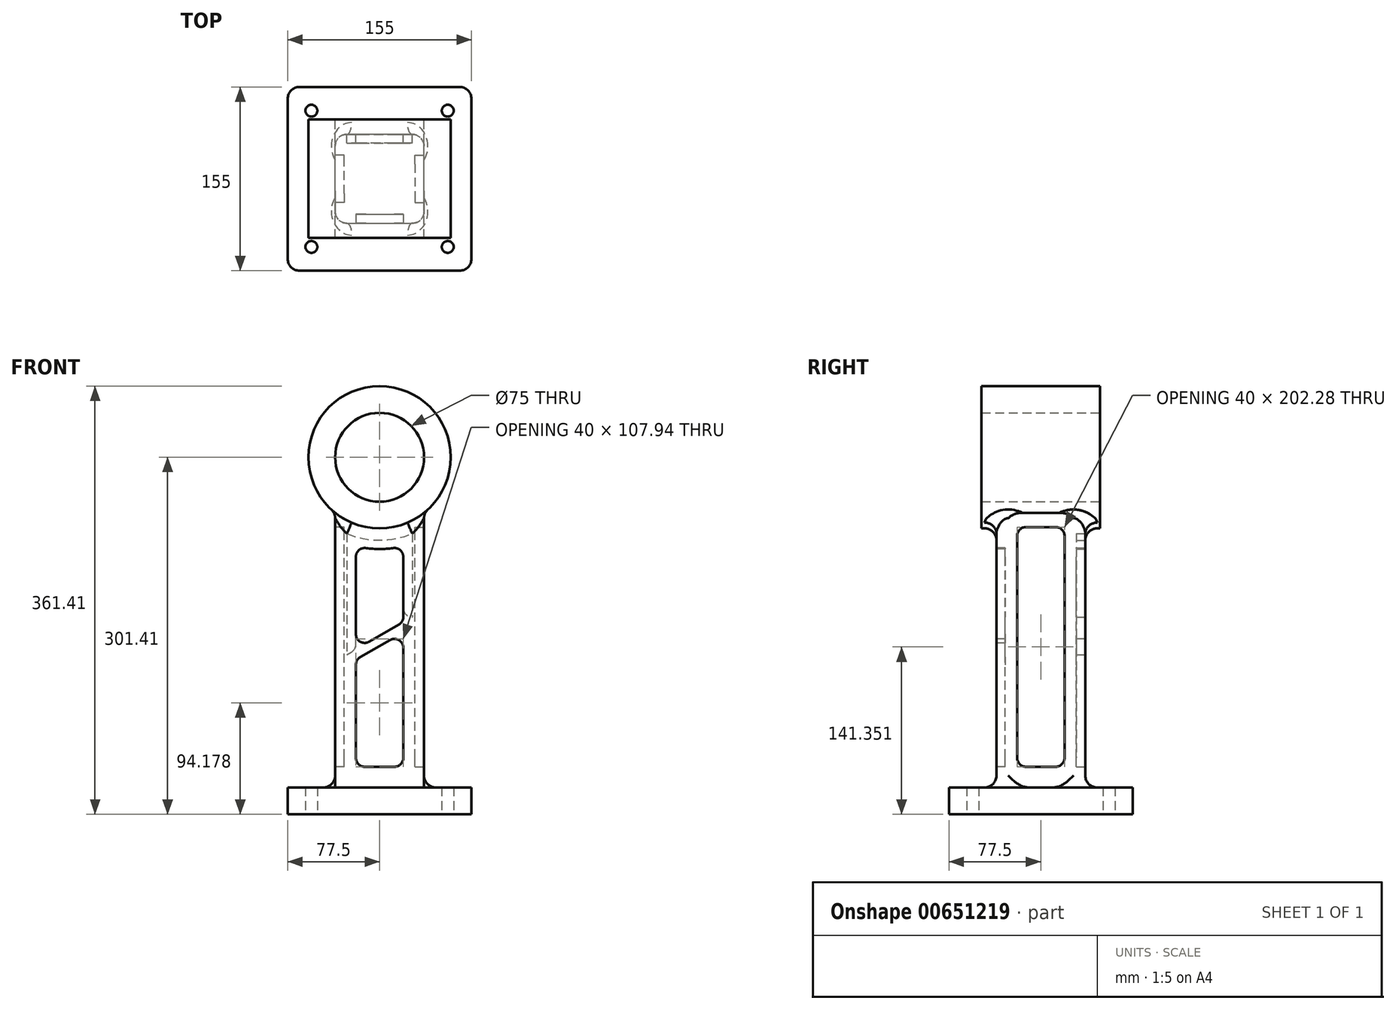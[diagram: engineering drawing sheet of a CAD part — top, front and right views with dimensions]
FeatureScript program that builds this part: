
annotation { "Feature Type Name" : "Feature", "Feature Type Description" : "" }
export const myFeature = defineFeature(function(context is Context, id is Id, definition is map)
    precondition{}
    {
        {
            var Q0;
            Q0=qCreatedBy(makeId("Front.planeOp"),FACE);
            var sketch = newSketch(context, id + "F0", { "sketchPlane" : qUnion([Q0])});
            skCircle(sketch, "E0", {"center": v(0, 0) * mm, "radius": 37.5 * mm});
            skCircle(sketch, "E1", {"center": v(0, 0) * mm, "radius": 60 * mm});
            skPoint(sketch, "E2", {"position": v(-37.5, 0) * mm});
            skPoint(sketch, "E3", {"position": v(37.5, 0) * mm});
            skPoint(sketch, "E4", {"position": v(-37.5, -46.84) * mm});
            skPoint(sketch, "E5", {"position": v(37.5, -46.84) * mm});
            skLineSegment(sketch, "E6", {"start": v(-37.5, -46.84) * mm, "end": v(-37.5, -278.7) * mm});
            skLineSegment(sketch, "E7", {"start": v(37.5, -46.84) * mm, "end": v(37.5, -278.7) * mm});
            skLineSegment(sketch, "E8", {"start": v(-37.5, -301.4) * mm, "end": v(37.5, -301.4) * mm});
            skLineSegment(sketch, "E9", {"start": v(37.5, -301.4) * mm, "end": v(77.5, -301.4) * mm});
            skLineSegment(sketch, "E10", {"start": v(77.5, -301.4) * mm, "end": v(77.5, -278.7) * mm});
            skLineSegment(sketch, "E11", {"start": v(77.5, -278.7) * mm, "end": v(37.5, -278.7) * mm});
            skLineSegment(sketch, "E12", {"start": v(37.5, -278.7) * mm, "end": v(-37.5, -278.7) * mm});
            skLineSegment(sketch, "E13", {"start": v(-37.5, -278.7) * mm, "end": v(-77.5, -278.7) * mm});
            skLineSegment(sketch, "E14", {"start": v(-77.5, -278.7) * mm, "end": v(-77.5, -301.4) * mm});
            skLineSegment(sketch, "E15", {"start": v(-77.5, -301.4) * mm, "end": v(-37.5, -301.4) * mm});
            skSolve(sketch);
        }
        {
            var Q0;
            Q0=makeQuery(id+"F0.imprint","IMPRINT",FACE,{"disambiguationData":[TD([[makeQuery(id+"F0.imprint","IMPRINT",EDGE,{"derivedFrom":sQuery(id+"F0.wireOp",EDGE,"E0")}),-1.0]])]});
            extrude(context, id + "F1", {"entities" : qUnion([Q0]), "endBound" : BoundingType.SYMMETRIC, "depth" : 100 * mm, "offsetDistance" : 25 * mm});
        }
        {
            var Q0;
            Q0 = qSketchRegion(id + "F0", true);
            extrude(context, id + "F2", {"entities" : qUnion([Q0]), "operationType" : NewBodyOperationType.ADD, "endBound" : BoundingType.SYMMETRIC, "depth" : 75 * mm, "offsetDistance" : 25 * mm});
        }
        {
            var Q0;
            Q0=makeQuery(id+"F2.opExtrude","CAP_FACE",FACE,{"disambiguationData":[OSD([sQuery(id+"F0.wireOp",EDGE,"E0"),sQuery(id+"F0.wireOp",EDGE,"E1"),sQuery(id+"F0.wireOp",EDGE,"E6"),sQuery(id+"F0.wireOp",EDGE,"E7"),sQuery(id+"F0.wireOp",EDGE,"E8"),sQuery(id+"F0.wireOp",EDGE,"E9"),sQuery(id+"F0.wireOp",EDGE,"E10"),sQuery(id+"F0.wireOp",EDGE,"E11"),sQuery(id+"F0.wireOp",EDGE,"E13"),sQuery(id+"F0.wireOp",EDGE,"E14"),sQuery(id+"F0.wireOp",EDGE,"E15")])],"isStart":false});
            var sketch = newSketch(context, id + "F3", { "sketchPlane" : qUnion([Q0])});
            skLineSegment(sketch, "E16", {"start": v(-37.5, -278.7) * mm, "end": v(37.5, -278.7) * mm});
            skSolve(sketch);
        }
        {
            var Q0;
            Q0=makeQuery(id+"F3.imprint","IMPRINT",FACE,{"disambiguationData":[TD([[makeQuery(id+"F3.imprint","IMPRINT",EDGE,{"derivedFrom":sQuery(id+"F3.wireOp",EDGE,"E16")}),-1.0]])]});
            extrude(context, id + "F4", {"entities" : qUnion([Q0]), "operationType" : NewBodyOperationType.ADD, "depth" : 40 * mm, "offsetDistance" : 25 * mm});
        }
        {
            var Q0;
            Q0=makeQuery(id+"F2.opExtrude","CAP_FACE",FACE,{"disambiguationData":[OSD([sQuery(id+"F0.wireOp",EDGE,"E0"),sQuery(id+"F0.wireOp",EDGE,"E1"),sQuery(id+"F0.wireOp",EDGE,"E6"),sQuery(id+"F0.wireOp",EDGE,"E7"),sQuery(id+"F0.wireOp",EDGE,"E8"),sQuery(id+"F0.wireOp",EDGE,"E9"),sQuery(id+"F0.wireOp",EDGE,"E10"),sQuery(id+"F0.wireOp",EDGE,"E11"),sQuery(id+"F0.wireOp",EDGE,"E13"),sQuery(id+"F0.wireOp",EDGE,"E14"),sQuery(id+"F0.wireOp",EDGE,"E15")])],"isStart":true});
            var sketch = newSketch(context, id + "F5", { "sketchPlane" : qUnion([Q0])});
            skLineSegment(sketch, "E17", {"start": v(37.5, -278.7) * mm, "end": v(-37.5, -278.7) * mm});
            skSolve(sketch);
        }
        {
            var Q0;
            Q0 = qSketchRegion(id + "F5", true);
            var Q1;
            Q1=makeQuery(id+"F5.imprint","IMPRINT",FACE,{"disambiguationData":[TD([[makeQuery(id+"F5.imprint","IMPRINT",EDGE,{"derivedFrom":sQuery(id+"F5.wireOp",EDGE,"E17")}),1.0]])]});
            extrude(context, id + "F6", {"entities" : qUnion([Q0, Q1]), "operationType" : NewBodyOperationType.ADD, "depth" : 40 * mm, "offsetDistance" : 25 * mm});
        }
        {
            var Q0;
            Q0=makeQuery(id+"F6.opExtrude","CAP_EDGE",EDGE,{"disambiguationData":[OSD([sQuery(id+"F0.wireOp",EDGE,"E14")])],"isStart":false});
            var Q1;
            Q1=makeQuery(id+"F6.opExtrude","CAP_EDGE",EDGE,{"disambiguationData":[OSD([sQuery(id+"F0.wireOp",EDGE,"E10")])],"isStart":false});
            var Q2;
            Q2=makeQuery(id+"F4.opExtrude","CAP_EDGE",EDGE,{"disambiguationData":[OSD([sQuery(id+"F0.wireOp",EDGE,"E10")])],"isStart":false});
            var Q3;
            Q3=makeQuery(id+"F4.opExtrude","CAP_EDGE",EDGE,{"disambiguationData":[OSD([sQuery(id+"F0.wireOp",EDGE,"E14")])],"isStart":false});
            fillet(context, id + "F7", {"entities" : qUnion([Q0, Q1, Q2, Q3]), "radius" : 10 * mm, "tangentPropagation" : true, "allowEdgeOverflow" : false});
        }
        {
            var Q0;
            Q0=makeQuery(id+"F2.opExtrude","CAP_FACE",FACE,{"disambiguationData":[OSD([sQuery(id+"F0.wireOp",EDGE,"E0"),sQuery(id+"F0.wireOp",EDGE,"E1"),sQuery(id+"F0.wireOp",EDGE,"E6"),sQuery(id+"F0.wireOp",EDGE,"E7"),sQuery(id+"F0.wireOp",EDGE,"E8"),sQuery(id+"F0.wireOp",EDGE,"E9"),sQuery(id+"F0.wireOp",EDGE,"E10"),sQuery(id+"F0.wireOp",EDGE,"E11"),sQuery(id+"F0.wireOp",EDGE,"E13"),sQuery(id+"F0.wireOp",EDGE,"E14"),sQuery(id+"F0.wireOp",EDGE,"E15")])],"isStart":false});
            fillet(context, id + "F8", {"entities" : qUnion([Q0]), "radius" : 10 * mm, "tangentPropagation" : true, "allowEdgeOverflow" : false});
        }
        {
            var Q0;
            Q0=makeQuery(id+"F2.opExtrude","CAP_FACE",FACE,{"disambiguationData":[OSD([sQuery(id+"F0.wireOp",EDGE,"E0"),sQuery(id+"F0.wireOp",EDGE,"E1"),sQuery(id+"F0.wireOp",EDGE,"E6"),sQuery(id+"F0.wireOp",EDGE,"E7"),sQuery(id+"F0.wireOp",EDGE,"E8"),sQuery(id+"F0.wireOp",EDGE,"E9"),sQuery(id+"F0.wireOp",EDGE,"E10"),sQuery(id+"F0.wireOp",EDGE,"E11"),sQuery(id+"F0.wireOp",EDGE,"E13"),sQuery(id+"F0.wireOp",EDGE,"E14"),sQuery(id+"F0.wireOp",EDGE,"E15")])],"isStart":true});
            fillet(context, id + "F9", {"entities" : qUnion([Q0]), "radius" : 10 * mm, "tangentPropagation" : true, "allowEdgeOverflow" : false});
        }
        {
            var Q0;
            Q0=makeQuery(id+"F2.opExtrude","CAP_FACE",FACE,{"disambiguationData":[OSD([sQuery(id+"F0.wireOp",EDGE,"E0"),sQuery(id+"F0.wireOp",EDGE,"E1"),sQuery(id+"F0.wireOp",EDGE,"E6"),sQuery(id+"F0.wireOp",EDGE,"E7"),sQuery(id+"F0.wireOp",EDGE,"E8"),sQuery(id+"F0.wireOp",EDGE,"E9"),sQuery(id+"F0.wireOp",EDGE,"E10"),sQuery(id+"F0.wireOp",EDGE,"E11"),sQuery(id+"F0.wireOp",EDGE,"E13"),sQuery(id+"F0.wireOp",EDGE,"E14"),sQuery(id+"F0.wireOp",EDGE,"E15")])],"isStart":false});
            var sketch = newSketch(context, id + "F10", { "sketchPlane" : qUnion([Q0])});
            skLineSegment(sketch, "E18", {"start": v(-27.5, -166.54) * mm, "end": v(27.5, -134.78) * mm});
            skLineSegment(sketch, "E19", {"start": v(-20, -162.2) * mm, "end": v(-20, -77.5) * mm});
            skLineSegment(sketch, "E20", {"start": v(20, -77.5) * mm, "end": v(20, -139.11) * mm});
            skLineSegment(sketch, "E21", {"start": v(-27.5, -175.2) * mm, "end": v(27.5, -143.44) * mm});
            skArc(sketch, "E22.0", {"start": v(20, -74.87) * mm, "mid": v(0, -77.5) * mm, "end": v(-20, -74.87) * mm});
            skLineSegment(sketch, "E23", {"start": v(-20, -77.5) * mm, "end": v(-20, -74.87) * mm});
            skLineSegment(sketch, "E24", {"start": v(20, -77.5) * mm, "end": v(20, -74.87) * mm});
            skLineSegment(sketch, "E25", {"start": v(-20, -261.2) * mm, "end": v(20, -261.2) * mm});
            skLineSegment(sketch, "E26", {"start": v(20, -261.2) * mm, "end": v(20, -147.77) * mm});
            skLineSegment(sketch, "E27", {"start": v(-20, -261.2) * mm, "end": v(-20, -170.87) * mm});
            skSolve(sketch);
        }
        {
            var Q0;
            {var subQ1=sQuery(id+"F10.wireOp",EDGE,"E19");Q0=makeQuery(id+"F10.imprint","IMPRINT",FACE,{"disambiguationData":[TD([[makeQuery(id+"F10.imprint","IMPRINT",EDGE,{"derivedFrom":subQ1}),-1.0]])]});}
            var Q1;
            Q1=makeQuery(id+"F10.imprint","IMPRINT",FACE,{"disambiguationData":[TD([[makeQuery(id+"F10.imprint","IMPRINT",EDGE,{"derivedFrom":sQuery(id+"F10.wireOp",EDGE,"E25")}),1.0]])]});
            extrude(context, id + "F11", {"entities" : qUnion([Q0, Q1]), "operationType" : NewBodyOperationType.REMOVE, "oppositeDirection" : true, "depth" : 7.5 * mm, "offsetDistance" : 25 * mm});
        }
        {
            var Q0;
            Q0=makeQuery(id+"F11.boolean.opBoolean","COPY",EDGE,{"derivedFrom":makeQuery(id+"F11.opExtrude","SWEPT_EDGE",EDGE,{"disambiguationData":[OSD([sQuery(id+"F10.wireOp",EDGE,"E21"),sQuery(id+"F10.wireOp",EDGE,"E27")])]})});
            var Q1;
            Q1=makeQuery(id+"F11.boolean.opBoolean","COPY",EDGE,{"derivedFrom":makeQuery(id+"F11.opExtrude","SWEPT_EDGE",EDGE,{"disambiguationData":[OSD([sQuery(id+"F10.wireOp",EDGE,"E21"),sQuery(id+"F10.wireOp",EDGE,"E26")])]})});
            var Q2;
            Q2=makeQuery(id+"F11.boolean.opBoolean","COPY",EDGE,{"derivedFrom":makeQuery(id+"F11.opExtrude","SWEPT_EDGE",EDGE,{"disambiguationData":[OSD([sQuery(id+"F10.wireOp",EDGE,"E25"),sQuery(id+"F10.wireOp",EDGE,"E27")])]})});
            var Q3;
            Q3=makeQuery(id+"F11.boolean.opBoolean","COPY",EDGE,{"derivedFrom":makeQuery(id+"F11.opExtrude","SWEPT_EDGE",EDGE,{"disambiguationData":[OSD([sQuery(id+"F10.wireOp",EDGE,"E25"),sQuery(id+"F10.wireOp",EDGE,"E26")])]})});
            var Q4;
            Q4=makeQuery(id+"F11.boolean.opBoolean","COPY",EDGE,{"derivedFrom":makeQuery(id+"F11.opExtrude","SWEPT_EDGE",EDGE,{"disambiguationData":[OSD([sQuery(id+"F10.wireOp",EDGE,"E22.0"),sQuery(id+"F10.wireOp",EDGE,"E23")])]})});
            var Q5;
            Q5=makeQuery(id+"F11.boolean.opBoolean","COPY",EDGE,{"derivedFrom":makeQuery(id+"F11.opExtrude","SWEPT_EDGE",EDGE,{"disambiguationData":[OSD([sQuery(id+"F10.wireOp",EDGE,"E18"),sQuery(id+"F10.wireOp",EDGE,"E19")])]})});
            var Q6;
            Q6=makeQuery(id+"F11.boolean.opBoolean","COPY",EDGE,{"derivedFrom":makeQuery(id+"F11.opExtrude","SWEPT_EDGE",EDGE,{"disambiguationData":[OSD([sQuery(id+"F10.wireOp",EDGE,"E22.0"),sQuery(id+"F10.wireOp",EDGE,"E24")])]})});
            var Q7;
            Q7=makeQuery(id+"F11.boolean.opBoolean","COPY",EDGE,{"derivedFrom":makeQuery(id+"F11.opExtrude","SWEPT_EDGE",EDGE,{"disambiguationData":[OSD([sQuery(id+"F10.wireOp",EDGE,"E18"),sQuery(id+"F10.wireOp",EDGE,"E20")])]})});
            fillet(context, id + "F12", {"entities" : qUnion([Q0, Q1, Q2, Q3, Q4, Q5, Q6, Q7]), "radius" : 7.5 * mm, "tangentPropagation" : true, "allowEdgeOverflow" : false});
        }
        {
            var Q0;
            Q0=makeQuery(id+"F2.opExtrude","CAP_FACE",FACE,{"disambiguationData":[OSD([sQuery(id+"F0.wireOp",EDGE,"E0"),sQuery(id+"F0.wireOp",EDGE,"E1"),sQuery(id+"F0.wireOp",EDGE,"E6"),sQuery(id+"F0.wireOp",EDGE,"E7"),sQuery(id+"F0.wireOp",EDGE,"E8"),sQuery(id+"F0.wireOp",EDGE,"E9"),sQuery(id+"F0.wireOp",EDGE,"E10"),sQuery(id+"F0.wireOp",EDGE,"E11"),sQuery(id+"F0.wireOp",EDGE,"E13"),sQuery(id+"F0.wireOp",EDGE,"E14"),sQuery(id+"F0.wireOp",EDGE,"E15")])],"isStart":true});
            var sketch = newSketch(context, id + "F13", { "sketchPlane" : qUnion([Q0])});
            skLineSegment(sketch, "E28", {"start": v(27.5, -166.54) * mm, "end": v(-27.5, -134.78) * mm});
            skArc(sketch, "E29.0", {"start": v(20, -74.87) * mm, "mid": v(0, -77.5) * mm, "end": v(-20, -74.87) * mm});
            skLineSegment(sketch, "E30", {"start": v(-20, -139.11) * mm, "end": v(-20, -74.87) * mm});
            skLineSegment(sketch, "E31", {"start": v(20, -162.2) * mm, "end": v(20, -74.87) * mm});
            skLineSegment(sketch, "E32", {"start": v(27.5, -175.2) * mm, "end": v(-27.5, -143.44) * mm});
            skLineSegment(sketch, "E33", {"start": v(-20, -147.77) * mm, "end": v(-20, -261.2) * mm});
            skLineSegment(sketch, "E34", {"start": v(-20, -261.2) * mm, "end": v(20, -261.2) * mm});
            skLineSegment(sketch, "E35", {"start": v(20, -261.2) * mm, "end": v(20, -170.87) * mm});
            skSolve(sketch);
        }
        {
            var Q0;
            Q0=makeQuery(id+"F13.imprint","IMPRINT",FACE,{"disambiguationData":[TD([[makeQuery(id+"F13.imprint","IMPRINT",EDGE,{"derivedFrom":sQuery(id+"F13.wireOp",EDGE,"E29.0")}),1.0]])]});
            var Q1;
            {var subQ0=sQuery(id+"F13.wireOp",EDGE,"E33");Q1=makeQuery(id+"F13.imprint","IMPRINT",FACE,{"disambiguationData":[TD([[makeQuery(id+"F13.imprint","IMPRINT",EDGE,{"derivedFrom":subQ0}),1.0]])]});}
            extrude(context, id + "F14", {"entities" : qUnion([Q0, Q1]), "operationType" : NewBodyOperationType.REMOVE, "oppositeDirection" : true, "depth" : 7.5 * mm, "offsetDistance" : 25 * mm});
        }
        {
            var Q0;
            Q0=makeQuery(id+"F14.boolean.opBoolean","COPY",EDGE,{"derivedFrom":makeQuery(id+"F14.opExtrude","SWEPT_EDGE",EDGE,{"disambiguationData":[OSD([sQuery(id+"F13.wireOp",EDGE,"E28"),sQuery(id+"F13.wireOp",EDGE,"E30")])]})});
            var Q1;
            Q1=makeQuery(id+"F14.boolean.opBoolean","COPY",EDGE,{"derivedFrom":makeQuery(id+"F14.opExtrude","SWEPT_EDGE",EDGE,{"disambiguationData":[OSD([sQuery(id+"F13.wireOp",EDGE,"E33"),sQuery(id+"F13.wireOp",EDGE,"E34")])]})});
            var Q2;
            Q2=makeQuery(id+"F14.boolean.opBoolean","COPY",EDGE,{"derivedFrom":makeQuery(id+"F14.opExtrude","SWEPT_EDGE",EDGE,{"disambiguationData":[OSD([sQuery(id+"F13.wireOp",EDGE,"E32"),sQuery(id+"F13.wireOp",EDGE,"E33")])]})});
            var Q3;
            Q3=makeQuery(id+"F14.boolean.opBoolean","COPY",EDGE,{"derivedFrom":makeQuery(id+"F14.opExtrude","SWEPT_EDGE",EDGE,{"disambiguationData":[OSD([sQuery(id+"F13.wireOp",EDGE,"E29.0"),sQuery(id+"F13.wireOp",EDGE,"E30")])]})});
            var Q4;
            Q4=makeQuery(id+"F14.boolean.opBoolean","COPY",EDGE,{"derivedFrom":makeQuery(id+"F14.opExtrude","SWEPT_EDGE",EDGE,{"disambiguationData":[OSD([sQuery(id+"F13.wireOp",EDGE,"E32"),sQuery(id+"F13.wireOp",EDGE,"E35")])]})});
            var Q5;
            Q5=makeQuery(id+"F14.boolean.opBoolean","COPY",EDGE,{"derivedFrom":makeQuery(id+"F14.opExtrude","SWEPT_EDGE",EDGE,{"disambiguationData":[OSD([sQuery(id+"F13.wireOp",EDGE,"E29.0"),sQuery(id+"F13.wireOp",EDGE,"E31")])]})});
            var Q6;
            Q6=makeQuery(id+"F14.boolean.opBoolean","COPY",EDGE,{"derivedFrom":makeQuery(id+"F14.opExtrude","SWEPT_EDGE",EDGE,{"disambiguationData":[OSD([sQuery(id+"F13.wireOp",EDGE,"E34"),sQuery(id+"F13.wireOp",EDGE,"E35")])]})});
            var Q7;
            Q7=makeQuery(id+"F14.boolean.opBoolean","COPY",EDGE,{"derivedFrom":makeQuery(id+"F14.opExtrude","SWEPT_EDGE",EDGE,{"disambiguationData":[OSD([sQuery(id+"F13.wireOp",EDGE,"E28"),sQuery(id+"F13.wireOp",EDGE,"E31")])]})});
            fillet(context, id + "F15", {"entities" : qUnion([Q0, Q1, Q2, Q3, Q4, Q5, Q6, Q7]), "radius" : 7.5 * mm, "tangentPropagation" : true, "allowEdgeOverflow" : false});
        }
        {
            var Q0;
            Q0=makeQuery(id+"F2.opExtrude","SWEPT_FACE",FACE,{"disambiguationData":[OSD([sQuery(id+"F0.wireOp",EDGE,"E6")])]});
            var sketch = newSketch(context, id + "F16", { "sketchPlane" : qUnion([Q0])});
            skLineSegment(sketch, "E36.0", {"start": v(20, -58.92) * mm, "end": v(-20, -58.92) * mm});
            skLineSegment(sketch, "E36.1", {"start": v(20, -261.2) * mm, "end": v(20, -58.92) * mm});
            skLineSegment(sketch, "E36.2", {"start": v(-20, -261.2) * mm, "end": v(20, -261.2) * mm});
            skLineSegment(sketch, "E36.3", {"start": v(-20, -58.92) * mm, "end": v(-20, -261.2) * mm});
            skSolve(sketch);
        }
        {
            var Q0;
            Q0=makeQuery(id+"F16.imprint","IMPRINT",FACE,{"disambiguationData":[TD([[makeQuery(id+"F16.imprint","IMPRINT",EDGE,{"derivedFrom":sQuery(id+"F16.wireOp",EDGE,"E36.0")}),1.0]])]});
            extrude(context, id + "F17", {"entities" : qUnion([Q0]), "operationType" : NewBodyOperationType.REMOVE, "oppositeDirection" : true, "depth" : 7.5 * mm, "offsetDistance" : 25 * mm});
        }
        {
            var Q0;
            Q0=makeQuery(id+"F17.boolean.opBoolean","COPY",EDGE,{"derivedFrom":makeQuery(id+"F17.opExtrude","SWEPT_EDGE",EDGE,{"disambiguationData":[OSD([sQuery(id+"F16.wireOp",EDGE,"E36.0"),sQuery(id+"F16.wireOp",EDGE,"E36.3")])]})});
            var Q1;
            Q1=makeQuery(id+"F17.boolean.opBoolean","COPY",EDGE,{"derivedFrom":makeQuery(id+"F17.opExtrude","SWEPT_EDGE",EDGE,{"disambiguationData":[OSD([sQuery(id+"F16.wireOp",EDGE,"E36.0"),sQuery(id+"F16.wireOp",EDGE,"E36.1")])]})});
            var Q2;
            Q2=makeQuery(id+"F17.boolean.opBoolean","COPY",EDGE,{"derivedFrom":makeQuery(id+"F17.opExtrude","SWEPT_EDGE",EDGE,{"disambiguationData":[OSD([sQuery(id+"F16.wireOp",EDGE,"E36.2"),sQuery(id+"F16.wireOp",EDGE,"E36.3")])]})});
            var Q3;
            Q3=makeQuery(id+"F17.boolean.opBoolean","COPY",EDGE,{"derivedFrom":makeQuery(id+"F17.opExtrude","SWEPT_EDGE",EDGE,{"disambiguationData":[OSD([sQuery(id+"F16.wireOp",EDGE,"E36.1"),sQuery(id+"F16.wireOp",EDGE,"E36.2")])]})});
            fillet(context, id + "F18", {"entities" : qUnion([Q0, Q1, Q2, Q3]), "radius" : 7.5 * mm, "tangentPropagation" : true, "allowEdgeOverflow" : false});
        }
        {
            var Q0;
            Q0=makeQuery(id+"F2.opExtrude","SWEPT_FACE",FACE,{"disambiguationData":[OSD([sQuery(id+"F0.wireOp",EDGE,"E7")])]});
            var sketch = newSketch(context, id + "F19", { "sketchPlane" : qUnion([Q0])});
            skLineSegment(sketch, "E37.0", {"start": v(20, -58.92) * mm, "end": v(-20, -58.92) * mm});
            skLineSegment(sketch, "E37.1", {"start": v(20, -261.2) * mm, "end": v(20, -58.92) * mm});
            skLineSegment(sketch, "E37.2", {"start": v(-20, -261.2) * mm, "end": v(20, -261.2) * mm});
            skLineSegment(sketch, "E37.3", {"start": v(-20, -58.92) * mm, "end": v(-20, -261.2) * mm});
            skSolve(sketch);
        }
        {
            var Q0;
            Q0=makeQuery(id+"F19.imprint","IMPRINT",FACE,{"disambiguationData":[TD([[makeQuery(id+"F19.imprint","IMPRINT",EDGE,{"derivedFrom":sQuery(id+"F19.wireOp",EDGE,"E37.0")}),1.0]])]});
            extrude(context, id + "F20", {"entities" : qUnion([Q0]), "operationType" : NewBodyOperationType.REMOVE, "oppositeDirection" : true, "depth" : 7.5 * mm, "offsetDistance" : 25 * mm});
        }
        {
            var Q0;
            Q0=makeQuery(id+"F20.boolean.opBoolean","COPY",EDGE,{"derivedFrom":makeQuery(id+"F20.opExtrude","SWEPT_EDGE",EDGE,{"disambiguationData":[OSD([sQuery(id+"F19.wireOp",EDGE,"E37.0"),sQuery(id+"F19.wireOp",EDGE,"E37.3")])]})});
            var Q1;
            Q1=makeQuery(id+"F20.boolean.opBoolean","COPY",EDGE,{"derivedFrom":makeQuery(id+"F20.opExtrude","SWEPT_EDGE",EDGE,{"disambiguationData":[OSD([sQuery(id+"F19.wireOp",EDGE,"E37.0"),sQuery(id+"F19.wireOp",EDGE,"E37.1")])]})});
            var Q2;
            Q2=makeQuery(id+"F20.boolean.opBoolean","COPY",EDGE,{"derivedFrom":makeQuery(id+"F20.opExtrude","SWEPT_EDGE",EDGE,{"disambiguationData":[OSD([sQuery(id+"F19.wireOp",EDGE,"E37.2"),sQuery(id+"F19.wireOp",EDGE,"E37.3")])]})});
            var Q3;
            Q3=makeQuery(id+"F20.boolean.opBoolean","COPY",EDGE,{"derivedFrom":makeQuery(id+"F20.opExtrude","SWEPT_EDGE",EDGE,{"disambiguationData":[OSD([sQuery(id+"F19.wireOp",EDGE,"E37.1"),sQuery(id+"F19.wireOp",EDGE,"E37.2")])]})});
            fillet(context, id + "F21", {"entities" : qUnion([Q0, Q1, Q2, Q3]), "radius" : 7.5 * mm, "tangentPropagation" : true, "allowEdgeOverflow" : false});
        }
        {
            var Q0;
            {var subQ0=sQuery(id+"F0.wireOp",EDGE,"E15");var subQ1=sQuery(id+"F0.wireOp",EDGE,"E9");var subQ2=sQuery(id+"F0.wireOp",EDGE,"E8");Q0=makeQuery(id+"F6.boolean.opBoolean","MERGE",FACE,{"derivedFrom":[makeQuery(id+"F4.boolean.opBoolean","MERGE",FACE,{"derivedFrom":[makeQuery(id+"F2.opExtrude","SWEPT_FACE",FACE,{"disambiguationData":[OSD([subQ2,subQ1,subQ0])]}),makeQuery(id+"F4.opExtrude","SWEPT_FACE",FACE,{"disambiguationData":[OSD([subQ2,subQ1,subQ0])]})]}),makeQuery(id+"F6.opExtrude","SWEPT_FACE",FACE,{"disambiguationData":[OSD([subQ2,subQ1,subQ0])]})]});}
            var sketch = newSketch(context, id + "F22", { "sketchPlane" : qUnion([Q0])});
            skLineSegment(sketch, "E38", {"start": v(-57.5, 77.5) * mm, "end": v(-57.5, 57.5) * mm, "construction": true});
            skLineSegment(sketch, "E39", {"start": v(-57.5, 57.5) * mm, "end": v(-77.5, 57.5) * mm, "construction": true});
            skCircle(sketch, "E40", {"center": v(-57.5, 57.5) * mm, "radius": 5 * mm});
            skLineSegment(sketch, "E41", {"start": v(-77.5, -57.5) * mm, "end": v(-57.5, -57.5) * mm, "construction": true});
            skLineSegment(sketch, "E42", {"start": v(-57.5, -57.5) * mm, "end": v(-57.5, -77.5) * mm, "construction": true});
            skLineSegment(sketch, "E43", {"start": v(57.5, -77.5) * mm, "end": v(57.5, -57.5) * mm, "construction": true});
            skLineSegment(sketch, "E44", {"start": v(57.5, -57.5) * mm, "end": v(77.5, -57.5) * mm, "construction": true});
            skLineSegment(sketch, "E45", {"start": v(57.5, 77.5) * mm, "end": v(57.5, 57.5) * mm, "construction": true});
            skLineSegment(sketch, "E46", {"start": v(57.5, 57.5) * mm, "end": v(77.5, 57.5) * mm, "construction": true});
            skCircle(sketch, "E47", {"center": v(-57.5, -57.5) * mm, "radius": 5 * mm});
            skCircle(sketch, "E48", {"center": v(57.5, -57.5) * mm, "radius": 5 * mm});
            skCircle(sketch, "E49", {"center": v(57.5, 57.5) * mm, "radius": 5 * mm});
            skSolve(sketch);
        }
        {
            var Q0;
            Q0=makeQuery(id+"F22.imprint","IMPRINT",FACE,{"disambiguationData":[TD([[makeQuery(id+"F22.imprint","IMPRINT",EDGE,{"derivedFrom":sQuery(id+"F22.wireOp",EDGE,"E40")}),1.0]])]});
            var Q1;
            Q1=makeQuery(id+"F22.imprint","IMPRINT",FACE,{"disambiguationData":[TD([[makeQuery(id+"F22.imprint","IMPRINT",EDGE,{"derivedFrom":sQuery(id+"F22.wireOp",EDGE,"E49")}),1.0]])]});
            var Q2;
            Q2=makeQuery(id+"F22.imprint","IMPRINT",FACE,{"disambiguationData":[TD([[makeQuery(id+"F22.imprint","IMPRINT",EDGE,{"derivedFrom":sQuery(id+"F22.wireOp",EDGE,"E47")}),1.0]])]});
            var Q3;
            Q3=makeQuery(id+"F22.imprint","IMPRINT",FACE,{"disambiguationData":[TD([[makeQuery(id+"F22.imprint","IMPRINT",EDGE,{"derivedFrom":sQuery(id+"F22.wireOp",EDGE,"E48")}),1.0]])]});
            extrude(context, id + "F23", {"entities" : qUnion([Q0, Q1, Q2, Q3]), "operationType" : NewBodyOperationType.REMOVE, "oppositeDirection" : true, "depth" : 25 * mm, "offsetDistance" : 25 * mm});
        }
    });
